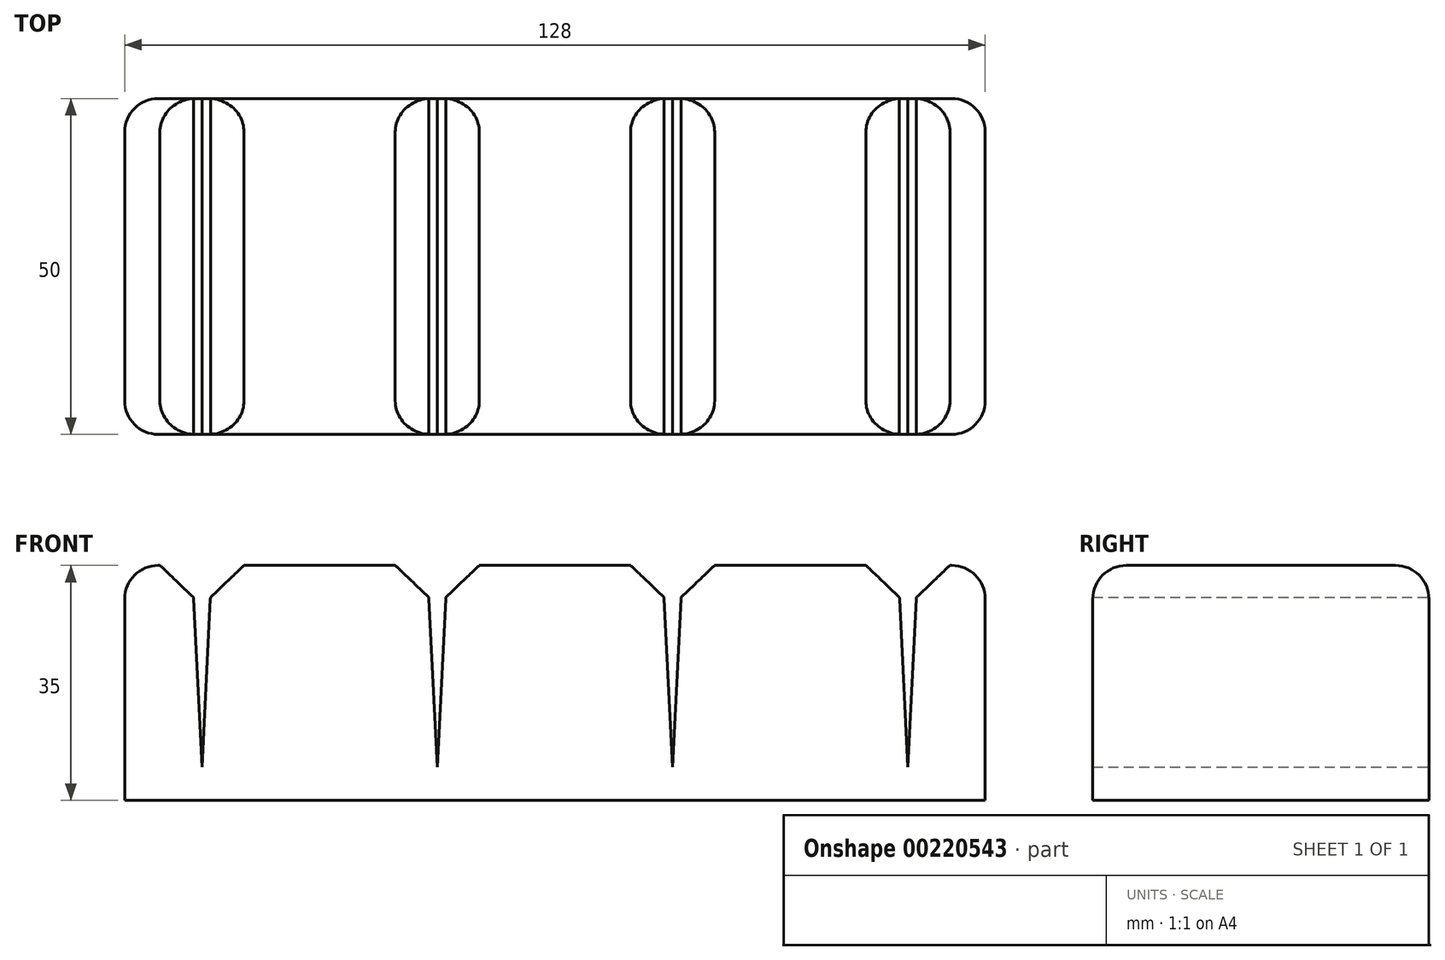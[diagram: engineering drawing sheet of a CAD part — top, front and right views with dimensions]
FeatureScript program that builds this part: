
annotation { "Feature Type Name" : "Feature", "Feature Type Description" : "" }
export const myFeature = defineFeature(function(context is Context, id is Id, definition is map)
    precondition{}
    {
        {
            var Q0;
            Q0=qCreatedBy(makeId("Front.planeOp"),FACE);
            var sketch = newSketch(context, id + "F0", { "sketchPlane" : qUnion([Q0])});
            skLineSegment(sketch, "E0.bottom", {"start": v(-62.64, -20.24) * mm, "end": v(65.36, -20.24) * mm});
            skLineSegment(sketch, "E0.top", {"start": v(-62.64, 14.76) * mm, "end": v(-52.64, 14.76) * mm});
            skLineSegment(sketch, "E0.left", {"start": v(-62.64, -20.24) * mm, "end": v(-62.64, 14.76) * mm});
            skLineSegment(sketch, "E0.right", {"start": v(65.36, -20.24) * mm, "end": v(65.36, 14.76) * mm});
            skLineSegment(sketch, "E1", {"start": v(-52.64, 14.76) * mm, "end": v(-51.14, -15.24) * mm});
            skLineSegment(sketch, "E2", {"start": v(-51.14, -15.24) * mm, "end": v(-49.64, 14.76) * mm});
            skLineSegment(sketch, "E3.1.0.0", {"start": v(-17.64, 14.76) * mm, "end": v(-16.14, -15.24) * mm});
            skLineSegment(sketch, "E3.1.0.1", {"start": v(-16.14, -15.24) * mm, "end": v(-14.64, 14.76) * mm});
            skLineSegment(sketch, "E3.2.0.0", {"start": v(17.36, 14.76) * mm, "end": v(18.86, -15.24) * mm});
            skLineSegment(sketch, "E3.2.0.1", {"start": v(18.86, -15.24) * mm, "end": v(20.36, 14.76) * mm});
            skLineSegment(sketch, "E3.3.0.0", {"start": v(52.36, 14.76) * mm, "end": v(53.86, -15.24) * mm});
            skLineSegment(sketch, "E3.3.0.1", {"start": v(53.86, -15.24) * mm, "end": v(55.36, 14.76) * mm});
            skLineSegment(sketch, "E3.direction1", {"start": v(-51.14, -15.24) * mm, "end": v(-16.14, -15.24) * mm, "construction": true});
            skLineSegment(sketch, "E4.trimOffspring", {"start": v(-49.64, 14.76) * mm, "end": v(-17.64, 14.76) * mm});
            skLineSegment(sketch, "E5.trimOffspring", {"start": v(-14.64, 14.76) * mm, "end": v(17.36, 14.76) * mm});
            skLineSegment(sketch, "E6.trimOffspring", {"start": v(20.36, 14.76) * mm, "end": v(52.36, 14.76) * mm});
            skLineSegment(sketch, "E7.trimOffspring", {"start": v(55.36, 14.76) * mm, "end": v(65.36, 14.76) * mm});
            skSolve(sketch);
        }
        {
            var Q0;
            Q0=makeQuery(id+"F0.imprint","IMPRINT",FACE,{"disambiguationData":[TD([[makeQuery(id+"F0.imprint","IMPRINT",EDGE,{"derivedFrom":sQuery(id+"F0.wireOp",EDGE,"E0.bottom")}),1.0]])]});
            extrude(context, id + "F1", {"entities" : qUnion([Q0]), "depth" : 50 * mm});
        }
        {
            var Q0;
            Q0=makeQuery(id+"F1.opExtrude","SWEPT_EDGE",EDGE,{"disambiguationData":[OSD([sQuery(id+"F0.wireOp",EDGE,"E0.top"),sQuery(id+"F0.wireOp",EDGE,"E1")])]});
            var Q1;
            Q1=makeQuery(id+"F1.opExtrude","SWEPT_EDGE",EDGE,{"disambiguationData":[OSD([sQuery(id+"F0.wireOp",EDGE,"E2"),sQuery(id+"F0.wireOp",EDGE,"E4.trimOffspring")])]});
            var Q2;
            Q2=makeQuery(id+"F1.opExtrude","SWEPT_EDGE",EDGE,{"disambiguationData":[OSD([sQuery(id+"F0.wireOp",EDGE,"E3.1.0.0"),sQuery(id+"F0.wireOp",EDGE,"E4.trimOffspring")])]});
            var Q3;
            Q3=makeQuery(id+"F1.opExtrude","SWEPT_EDGE",EDGE,{"disambiguationData":[OSD([sQuery(id+"F0.wireOp",EDGE,"E3.1.0.1"),sQuery(id+"F0.wireOp",EDGE,"E5.trimOffspring")])]});
            var Q4;
            Q4=makeQuery(id+"F1.opExtrude","SWEPT_EDGE",EDGE,{"disambiguationData":[OSD([sQuery(id+"F0.wireOp",EDGE,"E3.2.0.0"),sQuery(id+"F0.wireOp",EDGE,"E5.trimOffspring")])]});
            var Q5;
            Q5=makeQuery(id+"F1.opExtrude","SWEPT_EDGE",EDGE,{"disambiguationData":[OSD([sQuery(id+"F0.wireOp",EDGE,"E3.2.0.1"),sQuery(id+"F0.wireOp",EDGE,"E6.trimOffspring")])]});
            var Q6;
            Q6=makeQuery(id+"F1.opExtrude","SWEPT_EDGE",EDGE,{"disambiguationData":[OSD([sQuery(id+"F0.wireOp",EDGE,"E3.3.0.0"),sQuery(id+"F0.wireOp",EDGE,"E6.trimOffspring")])]});
            var Q7;
            Q7=makeQuery(id+"F1.opExtrude","SWEPT_EDGE",EDGE,{"disambiguationData":[OSD([sQuery(id+"F0.wireOp",EDGE,"E3.3.0.1"),sQuery(id+"F0.wireOp",EDGE,"E7.trimOffspring")])]});
            chamfer(context, id + "F2", {"entities" : qUnion([Q0, Q1, Q2, Q3, Q4, Q5, Q6, Q7]), "width" : 5 * mm, "tangentPropagation" : true});
        }
        {
            var Q0;
            Q0=makeQuery(id+"F1.opExtrude","SWEPT_EDGE",EDGE,{"disambiguationData":[OSD([sQuery(id+"F0.wireOp",EDGE,"E0.top"),sQuery(id+"F0.wireOp",EDGE,"E0.left")])]});
            var Q1;
            Q1=makeQuery(id+"F1.opExtrude","CAP_EDGE",EDGE,{"disambiguationData":[OSD([sQuery(id+"F0.wireOp",EDGE,"E0.top")])],"isStart":false});
            var Q2;
            Q2=makeQuery(id+"F1.opExtrude","CAP_EDGE",EDGE,{"disambiguationData":[OSD([sQuery(id+"F0.wireOp",EDGE,"E0.top")])],"isStart":true});
            var Q3;
            Q3=makeQuery(id+"F1.opExtrude","CAP_EDGE",EDGE,{"disambiguationData":[OSD([sQuery(id+"F0.wireOp",EDGE,"E4.trimOffspring")])],"isStart":false});
            var Q4;
            Q4=makeQuery(id+"F1.opExtrude","CAP_EDGE",EDGE,{"disambiguationData":[OSD([sQuery(id+"F0.wireOp",EDGE,"E4.trimOffspring")])],"isStart":true});
            var Q5;
            Q5=makeQuery(id+"F1.opExtrude","CAP_EDGE",EDGE,{"disambiguationData":[OSD([sQuery(id+"F0.wireOp",EDGE,"E5.trimOffspring")])],"isStart":true});
            var Q6;
            Q6=makeQuery(id+"F1.opExtrude","CAP_EDGE",EDGE,{"disambiguationData":[OSD([sQuery(id+"F0.wireOp",EDGE,"E5.trimOffspring")])],"isStart":false});
            var Q7;
            Q7=makeQuery(id+"F1.opExtrude","CAP_EDGE",EDGE,{"disambiguationData":[OSD([sQuery(id+"F0.wireOp",EDGE,"E6.trimOffspring")])],"isStart":false});
            var Q8;
            Q8=makeQuery(id+"F1.opExtrude","CAP_EDGE",EDGE,{"disambiguationData":[OSD([sQuery(id+"F0.wireOp",EDGE,"E6.trimOffspring")])],"isStart":true});
            var Q9;
            Q9=makeQuery(id+"F1.opExtrude","CAP_EDGE",EDGE,{"disambiguationData":[OSD([sQuery(id+"F0.wireOp",EDGE,"E7.trimOffspring")])],"isStart":false});
            var Q10;
            Q10=makeQuery(id+"F1.opExtrude","SWEPT_EDGE",EDGE,{"disambiguationData":[OSD([sQuery(id+"F0.wireOp",EDGE,"E0.right"),sQuery(id+"F0.wireOp",EDGE,"E7.trimOffspring")])]});
            var Q11;
            Q11=makeQuery(id+"F1.opExtrude","CAP_EDGE",EDGE,{"disambiguationData":[OSD([sQuery(id+"F0.wireOp",EDGE,"E7.trimOffspring")])],"isStart":true});
            var Q12;
            Q12=makeQuery(id+"F1.opExtrude","CAP_EDGE",EDGE,{"disambiguationData":[OSD([sQuery(id+"F0.wireOp",EDGE,"E0.left")])],"isStart":false});
            var Q13;
            Q13=makeQuery(id+"F1.opExtrude","CAP_EDGE",EDGE,{"disambiguationData":[OSD([sQuery(id+"F0.wireOp",EDGE,"E0.left")])],"isStart":true});
            var Q14;
            Q14=makeQuery(id+"F1.opExtrude","CAP_EDGE",EDGE,{"disambiguationData":[OSD([sQuery(id+"F0.wireOp",EDGE,"E0.right")])],"isStart":false});
            var Q15;
            Q15=makeQuery(id+"F1.opExtrude","CAP_EDGE",EDGE,{"disambiguationData":[OSD([sQuery(id+"F0.wireOp",EDGE,"E0.right")])],"isStart":true});
            fillet(context, id + "F3", {"entities" : qUnion([Q0, Q1, Q2, Q3, Q4, Q5, Q6, Q7, Q8, Q9, Q10, Q11, Q12, Q13, Q14, Q15]), "radius" : 5 * mm, "tangentPropagation" : true, "allowEdgeOverflow" : false});
        }
    });
